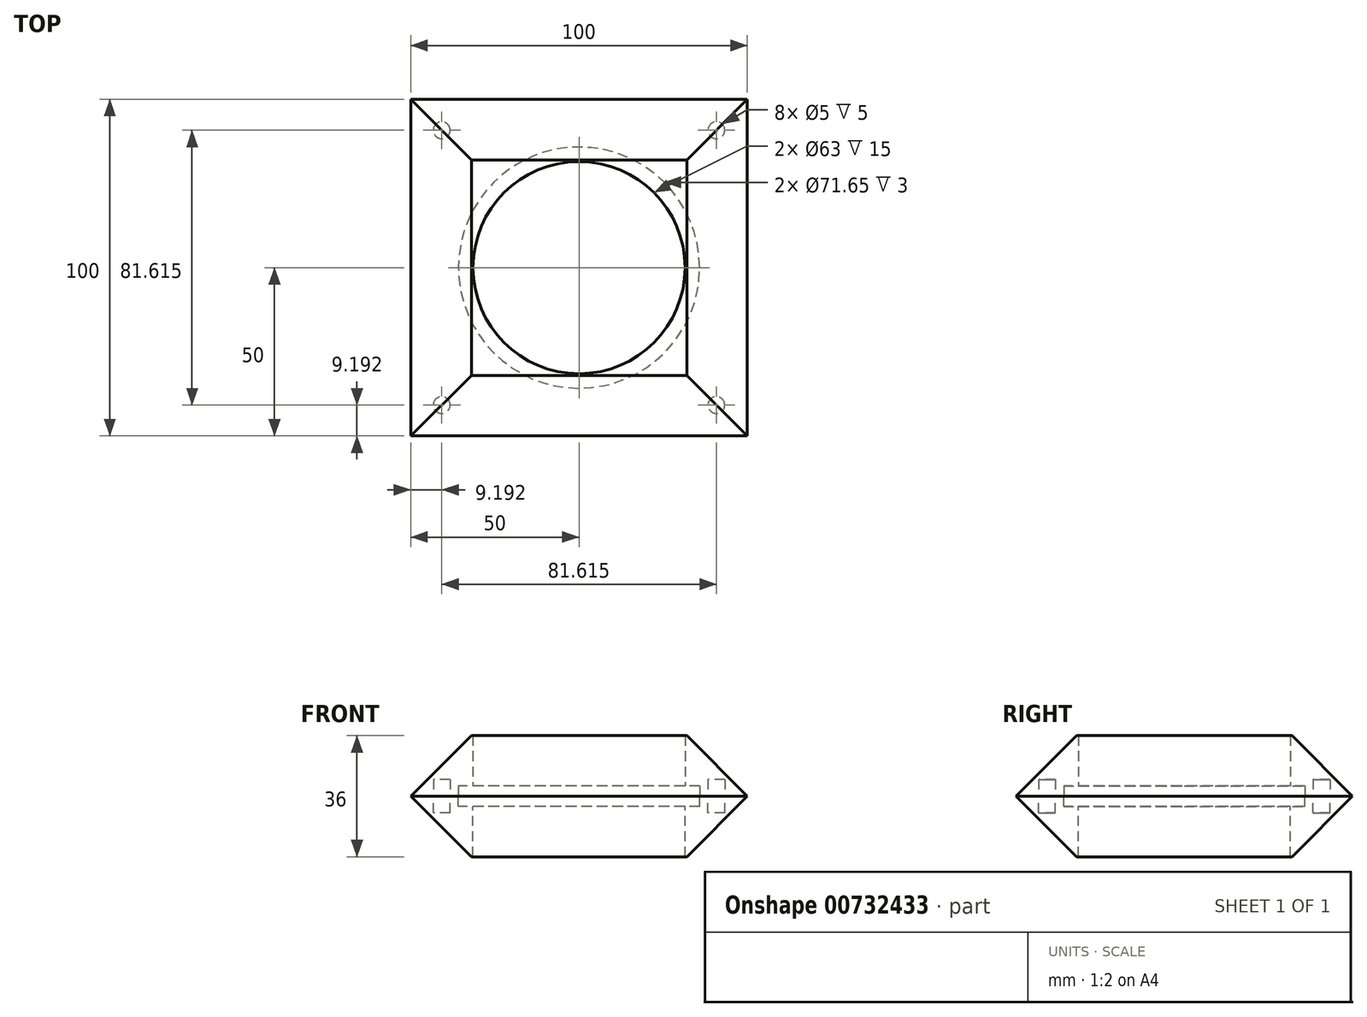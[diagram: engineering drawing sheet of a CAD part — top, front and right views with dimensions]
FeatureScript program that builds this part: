
annotation { "Feature Type Name" : "Feature", "Feature Type Description" : "" }
export const myFeature = defineFeature(function(context is Context, id is Id, definition is map)
    precondition{}
    {
        {
            var Q0;
            Q0=qCreatedBy(makeId("Top.planeOp"),FACE);
            var sketch = newSketch(context, id + "F0", { "sketchPlane" : qUnion([Q0])});
            skLineSegment(sketch, "E0.bottom", {"start": v(50, 50) * mm, "end": v(-50, 50) * mm});
            skLineSegment(sketch, "E0.top", {"start": v(50, -50) * mm, "end": v(-50, -50) * mm});
            skLineSegment(sketch, "E0.left", {"start": v(50, 50) * mm, "end": v(50, -50) * mm});
            skLineSegment(sketch, "E0.right", {"start": v(-50, 50) * mm, "end": v(-50, -50) * mm});
            skPoint(sketch, "E0.middle", {"position": v(0, 0) * mm});
            skSolve(sketch);
        }
        {
            var Q0;
            Q0 = qSketchRegion(id + "F0", true);
            extrude(context, id + "F1", {"entities" : qUnion([Q0]), "depth" : 18 * mm, "offsetDistance" : 25.4 * mm, "hasDraft" : true, "draftAngle" : 45 * degree, "draftPullDirection" : true});
        }
        {
            var Q0;
            Q0=qCreatedBy(makeId("Top.planeOp"),FACE);
            var sketch = newSketch(context, id + "F2", { "sketchPlane" : qUnion([Q0])});
            skCircle(sketch, "E1", {"center": v(0, 0) * mm, "radius": 31.5 * mm});
            skSolve(sketch);
        }
        {
            var Q0;
            Q0 = qSketchRegion(id + "F2", true);
            extrude(context, id + "F3", {"entities" : qUnion([Q0]), "operationType" : NewBodyOperationType.REMOVE, "depth" : 18 * mm, "offsetDistance" : 25.4 * mm});
        }
        {
            var Q0;
            Q0=qCreatedBy(makeId("Top.planeOp"),FACE);
            var sketch = newSketch(context, id + "F4", { "sketchPlane" : qUnion([Q0])});
            skCircle(sketch, "E2", {"center": v(0, 0) * mm, "radius": 35.83 * mm});
            skSolve(sketch);
        }
        {
            var Q0;
            Q0 = qSketchRegion(id + "F4", true);
            extrude(context, id + "F5", {"entities" : qUnion([Q0]), "operationType" : NewBodyOperationType.REMOVE, "depth" : 3 * mm, "offsetDistance" : 25.4 * mm});
        }
        {
            var Q0;
            Q0=qCreatedBy(makeId("Top.planeOp"),FACE);
            var sketch = newSketch(context, id + "F6", { "sketchPlane" : qUnion([Q0])});
            skCircle(sketch, "E3", {"center": v(-40.8, 40.8) * mm, "radius": 2.5 * mm});
            skCircle(sketch, "E4.0.1.0", {"center": v(-40.8, -40.8) * mm, "radius": 2.5 * mm});
            skCircle(sketch, "E4.1.0.0", {"center": v(40.8, 40.8) * mm, "radius": 2.5 * mm});
            skCircle(sketch, "E4.1.1.0", {"center": v(40.8, -40.8) * mm, "radius": 2.5 * mm});
            skLineSegment(sketch, "E4.direction1", {"start": v(-40.8, 40.8) * mm, "end": v(40.8, 40.8) * mm, "construction": true});
            skLineSegment(sketch, "E4.direction2", {"start": v(-40.8, 40.8) * mm, "end": v(-40.8, -40.8) * mm, "construction": true});
            skSolve(sketch);
        }
        {
            var Q0;
            Q0 = qSketchRegion(id + "F6", true);
            extrude(context, id + "F7", {"entities" : qUnion([Q0]), "operationType" : NewBodyOperationType.REMOVE, "depth" : 5 * mm, "offsetDistance" : 25.4 * mm});
        }
        {
            var Q0;
            Q0=makeQuery(id+"F1.opExtrude","SWEPT_BODY",BODY,{"disambiguationData":[OSD([sQuery(id+"F0.wireOp",EDGE,"E0.bottom"),sQuery(id+"F0.wireOp",EDGE,"E0.top"),sQuery(id+"F0.wireOp",EDGE,"E0.left"),sQuery(id+"F0.wireOp",EDGE,"E0.right")])]});
            var Q1;
            Q1=qCreatedBy(makeId("Top.planeOp"),FACE);
            mirror(context, id + "F8", {"entities" : qUnion([Q0]), "mirrorPlane" : qUnion([Q1])});
        }
    });
